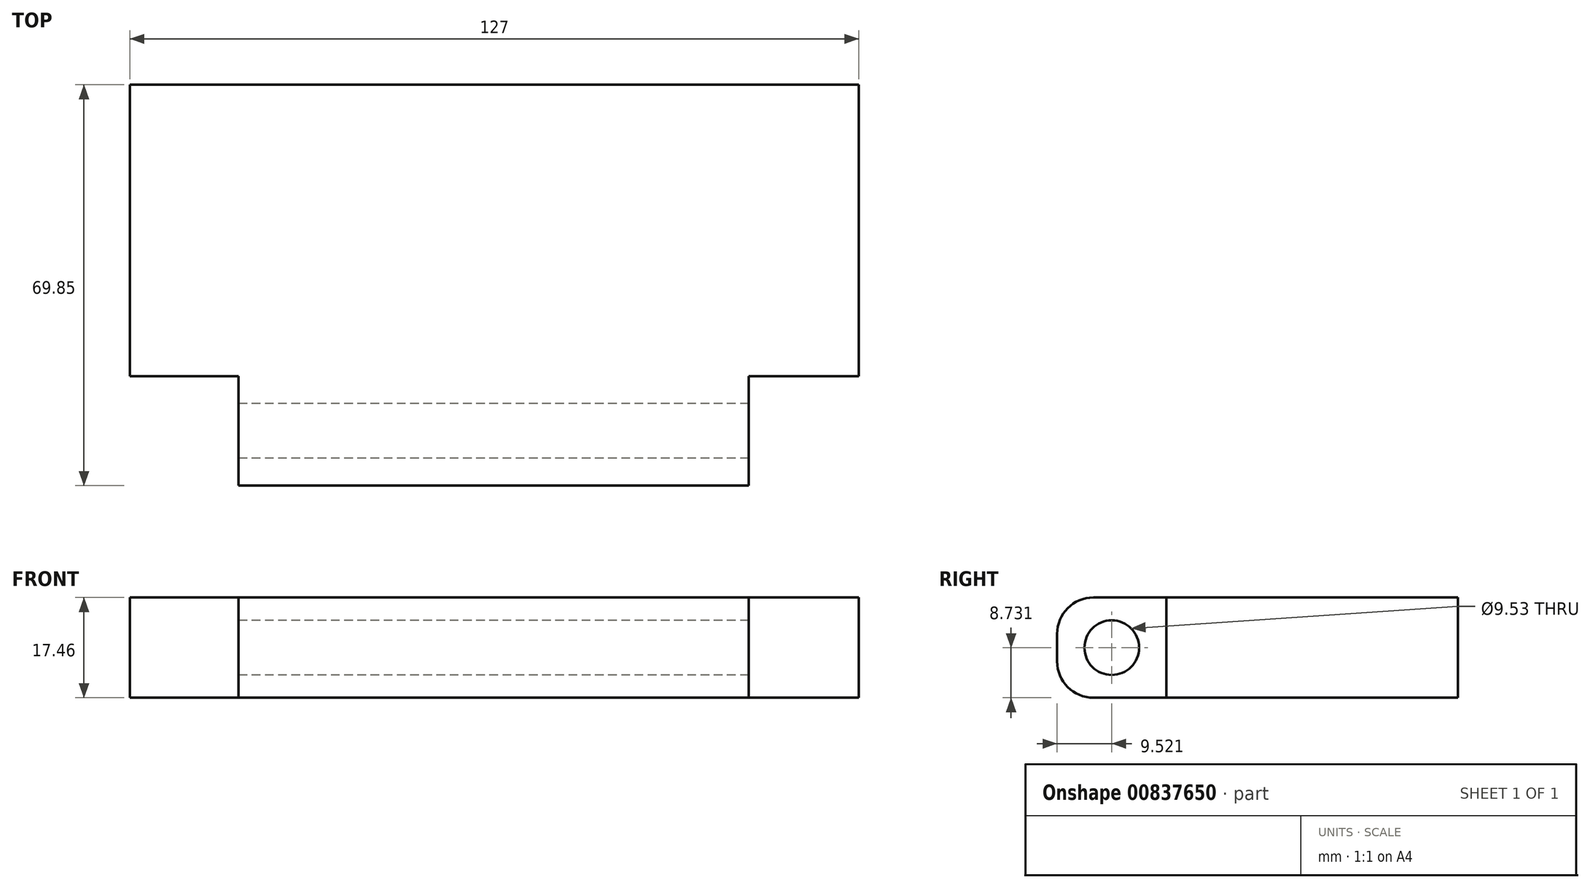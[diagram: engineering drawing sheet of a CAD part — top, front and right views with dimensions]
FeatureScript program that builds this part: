
annotation { "Feature Type Name" : "Feature", "Feature Type Description" : "" }
export const myFeature = defineFeature(function(context is Context, id is Id, definition is map)
    precondition{}
    {
        {
            var Q0;
            Q0=qCreatedBy(makeId("Top.planeOp"),FACE);
            var sketch = newSketch(context, id + "F0", { "sketchPlane" : qUnion([Q0])});
            skLineSegment(sketch, "E0", {"start": v(-64.3, 41.76) * mm, "end": v(62.7, 41.76) * mm});
            skLineSegment(sketch, "E1", {"start": v(62.7, 41.76) * mm, "end": v(62.7, -9.04) * mm});
            skLineSegment(sketch, "E2", {"start": v(62.7, -9.04) * mm, "end": v(43.55, -9.04) * mm});
            skLineSegment(sketch, "E3", {"start": v(43.55, -9.04) * mm, "end": v(43.55, -28.1) * mm});
            skLineSegment(sketch, "E4", {"start": v(43.55, -28.1) * mm, "end": v(-45.35, -28.1) * mm});
            skLineSegment(sketch, "E5", {"start": v(-45.35, -28.1) * mm, "end": v(-45.35, -9.04) * mm});
            skLineSegment(sketch, "E6", {"start": v(-45.35, -9.04) * mm, "end": v(-64.3, -9.04) * mm});
            skLineSegment(sketch, "E7", {"start": v(-64.3, -9.04) * mm, "end": v(-64.3, 41.76) * mm});
            skSolve(sketch);
        }
        {
            var Q0;
            Q0 = qSketchRegion(id + "F0", true);
            extrude(context, id + "F1", {"entities" : qUnion([Q0]), "depth" : 17.46 * mm, "offsetDistance" : 25.4 * mm});
        }
        {
            var Q0;
            Q0=makeQuery(id+"F1.opExtrude","SWEPT_FACE",FACE,{"disambiguationData":[OSD([sQuery(id+"F0.wireOp",EDGE,"E5")])]});
            var sketch = newSketch(context, id + "F2", { "sketchPlane" : qUnion([Q0])});
            skPoint(sketch, "E8", {"position": v(18.57, 8.73) * mm});
            skPoint(sketch, "E8.positionSnap0", {"position": v(28.1, 8.73) * mm});
            skPoint(sketch, "E8.positionSnap1", {"position": v(18.57, 0) * mm});
            skSolve(sketch);
        }
        {
            var Q0;
            Q0=sQuery(id+"F2.wireOp",VERTEX,"E8");
            var Q1;
            Q1=makeQuery(id+"F1.opExtrude","SWEPT_BODY",BODY,{"disambiguationData":[OSD([sQuery(id+"F0.wireOp",EDGE,"E0"),sQuery(id+"F0.wireOp",EDGE,"E1"),sQuery(id+"F0.wireOp",EDGE,"E2"),sQuery(id+"F0.wireOp",EDGE,"E3"),sQuery(id+"F0.wireOp",EDGE,"E4"),sQuery(id+"F0.wireOp",EDGE,"E5"),sQuery(id+"F0.wireOp",EDGE,"E6"),sQuery(id+"F0.wireOp",EDGE,"E7")])]});
            hole(context, id + "F3", {"style" : HoleStyle.SIMPLE, "endStyle" : HoleEndStyle.THROUGH, "holeDiameter" : 9.52 * mm, "majorDiameter" : 6.35 * mm, "isTappedThrough" : true, "tappedDepth" : 12.7 * mm, "tapClearance" : 3, "locations" : qUnion([Q0]), "scope" : qUnion([Q1])});
        }
        {
            var Q0;
            Q0=makeQuery(id+"F1.opExtrude","CAP_EDGE",EDGE,{"disambiguationData":[OSD([sQuery(id+"F0.wireOp",EDGE,"E4")])],"isStart":false});
            var Q1;
            Q1=makeQuery(id+"F1.opExtrude","CAP_EDGE",EDGE,{"disambiguationData":[OSD([sQuery(id+"F0.wireOp",EDGE,"E4")])],"isStart":true});
            fillet(context, id + "F4", {"entities" : qUnion([Q0, Q1]), "radius" : 6.35 * mm, "tangentPropagation" : true, "allowEdgeOverflow" : false});
        }
    });
